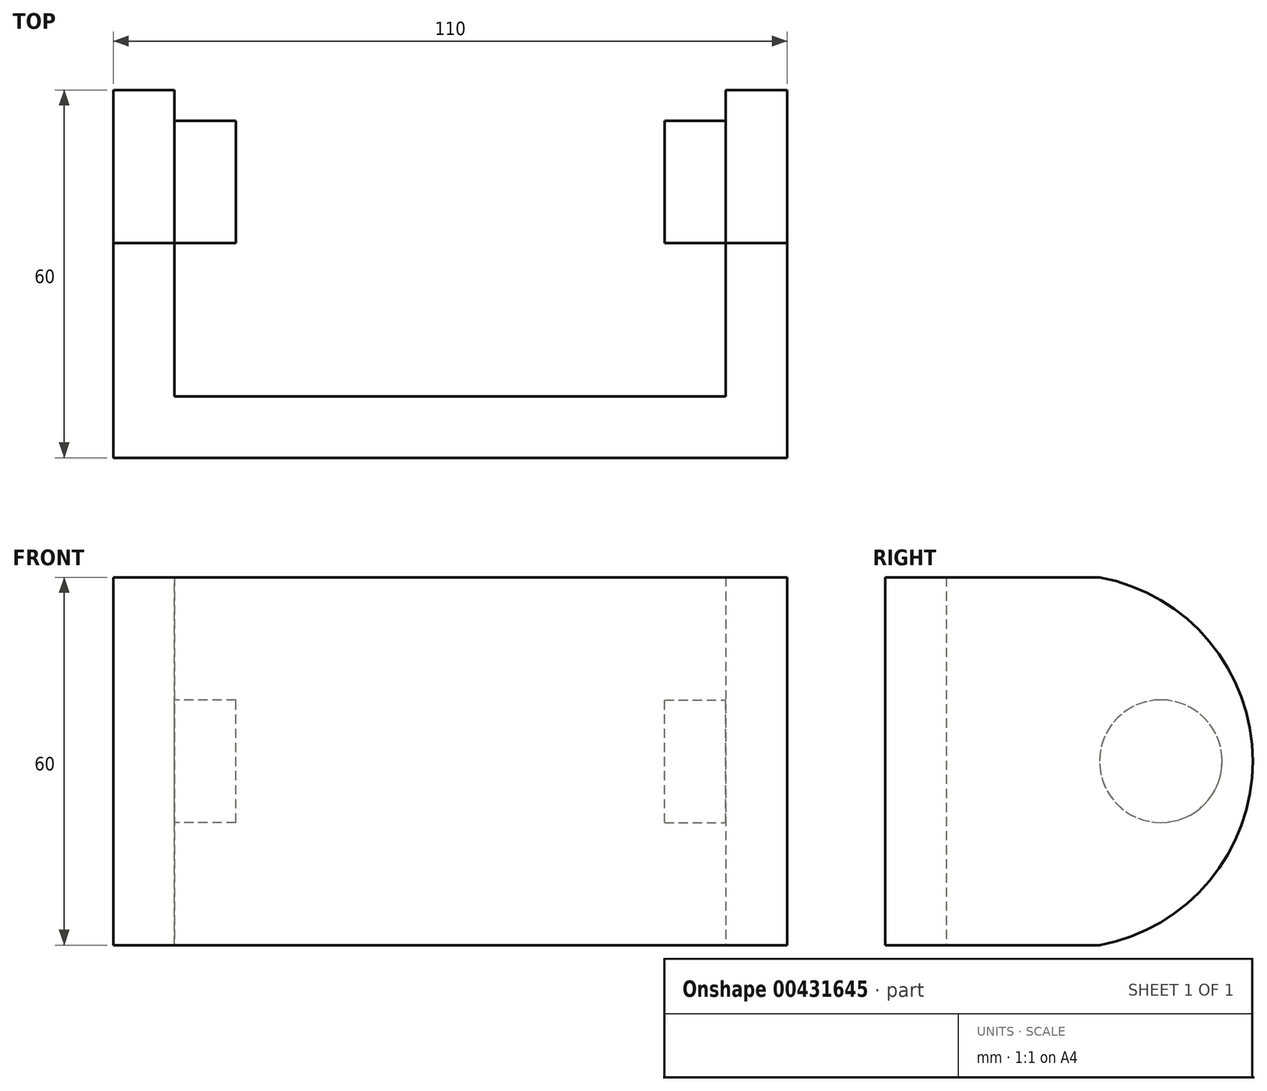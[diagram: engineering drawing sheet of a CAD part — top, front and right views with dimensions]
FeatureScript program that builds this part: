
annotation { "Feature Type Name" : "Feature", "Feature Type Description" : "" }
export const myFeature = defineFeature(function(context is Context, id is Id, definition is map)
    precondition{}
    {
        {
            var Q0;
            Q0=qCreatedBy(makeId("Top.planeOp"),FACE);
            var sketch = newSketch(context, id + "F0", { "sketchPlane" : qUnion([Q0])});
            skLineSegment(sketch, "E0.bottom", {"start": v(0, 0) * mm, "end": v(90, 0) * mm});
            skLineSegment(sketch, "E0.top", {"start": v(0, -50) * mm, "end": v(90, -50) * mm});
            skLineSegment(sketch, "E0.left", {"start": v(0, 0) * mm, "end": v(0, -50) * mm});
            skLineSegment(sketch, "E0.right", {"start": v(90, 0) * mm, "end": v(90, -50) * mm});
            skLineSegment(sketch, "E1", {"start": v(0, 0) * mm, "end": v(-10, 0) * mm});
            skLineSegment(sketch, "E2", {"start": v(-10, 0) * mm, "end": v(-10, -60) * mm});
            skLineSegment(sketch, "E3", {"start": v(-10, -60) * mm, "end": v(100, -60) * mm});
            skLineSegment(sketch, "E4", {"start": v(100, -60) * mm, "end": v(100, 0) * mm});
            skLineSegment(sketch, "E5", {"start": v(100, 0) * mm, "end": v(90, 0) * mm});
            skSolve(sketch);
        }
        {
            var Q0;
            Q0=makeQuery(id+"F0.imprint","IMPRINT",FACE,{"disambiguationData":[TD([[makeQuery(id+"F0.imprint","IMPRINT",EDGE,{"derivedFrom":sQuery(id+"F0.wireOp",EDGE,"E0.top")}),-1.0]])]});
            extrude(context, id + "F1", {"entities" : qUnion([Q0]), "depth" : 60 * mm});
        }
        {
            var Q0;
            Q0=makeQuery(id+"F1.opExtrude","SWEPT_FACE",FACE,{"disambiguationData":[OSD([sQuery(id+"F0.wireOp",EDGE,"E0.right")])]});
            var sketch = newSketch(context, id + "F2", { "sketchPlane" : qUnion([Q0])});
            skLineSegment(sketch, "E6", {"start": v(0, 0) * mm, "end": v(0, 30) * mm});
            skLineSegment(sketch, "E7", {"start": v(0, 30) * mm, "end": v(15, 30) * mm});
            skCircle(sketch, "E8", {"center": v(15, 30) * mm, "radius": 10 * mm});
            skArc(sketch, "E9", {"start": v(25, 60) * mm, "mid": v(0, 30) * mm, "end": v(25, 0) * mm});
            skSolve(sketch);
        }
        {
            var Q0;
            Q0=makeQuery(id+"F1.opExtrude","SWEPT_FACE",FACE,{"disambiguationData":[OSD([sQuery(id+"F0.wireOp",EDGE,"E0.left")])]});
            var sketch = newSketch(context, id + "F3", { "sketchPlane" : qUnion([Q0])});
            skLineSegment(sketch, "E10", {"start": v(0, 0) * mm, "end": v(0, 30) * mm});
            skLineSegment(sketch, "E11", {"start": v(0, 30) * mm, "end": v(-15, 30) * mm});
            skCircle(sketch, "E12", {"center": v(-15, 30) * mm, "radius": 10 * mm});
            skSolve(sketch);
        }
        {
            var Q0;
            Q0=makeQuery(id+"F2.imprint","IMPRINT",FACE,{"disambiguationData":[TD([[makeQuery(id+"F2.imprint","IMPRINT",EDGE,{"derivedFrom":sQuery(id+"F2.wireOp",EDGE,"E8")}),1.0]])]});
            extrude(context, id + "F4", {"entities" : qUnion([Q0]), "operationType" : NewBodyOperationType.ADD, "depth" : 10 * mm});
        }
        {
            var Q0;
            Q0=makeQuery(id+"F3.imprint","IMPRINT",FACE,{"disambiguationData":[TD([[makeQuery(id+"F3.imprint","IMPRINT",EDGE,{"derivedFrom":sQuery(id+"F3.wireOp",EDGE,"E12")}),1.0]])]});
            extrude(context, id + "F5", {"entities" : qUnion([Q0]), "operationType" : NewBodyOperationType.ADD, "depth" : 10 * mm});
        }
        {
            var Q0;
            {var subQ0=sQuery(id+"F2.wireOp",EDGE,"E9");var subQ1=sQuery(id+"F0.wireOp",EDGE,"E0.right");var subQ4=makeQuery(id+"F1.opExtrude","CAP_EDGE",EDGE,{"disambiguationData":[OSD([subQ1])],"isStart":false});var subQ5=makeQuery(id+"F2.imprint","INTERSECT",VERTEX,{"derivedFrom":[subQ4,subQ0]});Q0=makeQuery(id+"F2.imprint","IMPRINT",FACE,{"disambiguationData":[TD([[makeQuery(id+"F2.imprint","IMPRINT",EDGE,{"disambiguationData":[TD([[subQ5,1.0]])],"derivedFrom":subQ4}),-1.0]])]});}
            var Q1;
            {var subQ0=sQuery(id+"F2.wireOp",EDGE,"E6");Q1=makeQuery(id+"F2.imprint","IMPRINT",FACE,{"disambiguationData":[TD([[makeQuery(id+"F2.imprint","IMPRINT",EDGE,{"derivedFrom":subQ0}),1.0]])]});}
            extrude(context, id + "F6", {"entities" : qUnion([Q0, Q1]), "operationType" : NewBodyOperationType.REMOVE, "oppositeDirection" : true, "depth" : 25 * mm});
        }
        {
            var Q0;
            {var subQ0=sQuery(id+"F2.wireOp",EDGE,"E9");var subQ1=sQuery(id+"F0.wireOp",EDGE,"E0.right");var subQ4=makeQuery(id+"F1.opExtrude","CAP_EDGE",EDGE,{"disambiguationData":[OSD([subQ1])],"isStart":false});var subQ5=makeQuery(id+"F2.imprint","INTERSECT",VERTEX,{"derivedFrom":[subQ4,subQ0]});Q0=makeQuery(id+"F2.imprint","IMPRINT",FACE,{"disambiguationData":[TD([[makeQuery(id+"F2.imprint","IMPRINT",EDGE,{"disambiguationData":[TD([[subQ5,1.0]])],"derivedFrom":subQ4}),-1.0]])]});}
            var Q1;
            {var subQ0=sQuery(id+"F2.wireOp",EDGE,"E6");Q1=makeQuery(id+"F2.imprint","IMPRINT",FACE,{"disambiguationData":[TD([[makeQuery(id+"F2.imprint","IMPRINT",EDGE,{"derivedFrom":subQ0}),1.0]])]});}
            extrude(context, id + "F7", {"entities" : qUnion([Q0, Q1]), "operationType" : NewBodyOperationType.REMOVE, "depth" : 1000 * mm});
        }
    });
